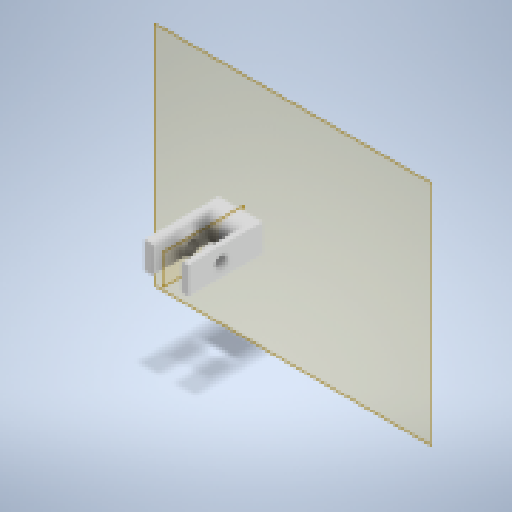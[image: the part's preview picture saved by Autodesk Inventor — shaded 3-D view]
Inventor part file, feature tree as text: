
AUTODESK INVENTOR PART (.ipt)
format: ipt  version: 2024 (Build 280153000, 153)  size: 782,848 bytes
history: native  units: mm
features: extrude x6, sketch x6, projected_geometry x5, other x5, fillet x4, reference x3, plane x2, direct_edit x1, move_body x1
ambient origin geometry x8: Origin, YZ Plane, XZ Plane, XY Plane, X Axis, Y Axis, Z Axis, Center Point
bodies: Solid1 (feature_tree)
feature tree (33):
  plane  "Work Plane1"
  extrude  "Extrusion1"  Depth=2.0mm TaperAngle=0.0deg
  extrude  "Extrusion2"  Depth=0.2mm
  extrude  "Extrusion3"  Depth=10.0mm
  fillet  "Fillet2"  Radius=10.0mm
  fillet  "Fillet3"  Radius=2.6mm
  extrude  "Extrusion4"  Depth=4.0mm
  extrude  "Extrusion5"  Depth=0.3mm
  fillet  "Fillet4"  Radius=2.0mm
  plane  "Work Plane2"
  extrude  "Extrusion6"  Depth=2.75mm
  fillet  "Fillet5"  [1 undecoded]
  direct_edit  "Direct Edit1"
  sketch  "Sketch1"  dims[d4=8.0mm d5=0.0mm d6=2.0mm d7=0.0mm]
  reference  "Reference1"
  sketch  "Sketch2"  dims[d11=0.4mm d12=0.2mm]
  projected_geometry  "Projected Loop1"
  reference  "Reference2"
  sketch  "Sketch3"  dims[d13=2.0mm d14=10.0mm d15=10.0mm d16=2.6mm]
  projected_geometry  "Projected Loop2"
  sketch  "Sketch4"  dims[d17=19.0mm d18=0.0mm d19=4.0mm]
  projected_geometry  "Projected Loop3"
  reference  "Reference3"
  sketch  "Sketch5"  dims[d20=1.0mm d21=0.3mm d22=2.0mm]
  projected_geometry  "Projected Loop4"
  sketch  "Sketch6"  dims[d23=3.9mm d25=5.0mm d26=0.0mm d27=0.0mm d28=11.7mm d29=1.5mm d30=2.0mm d31=0.0mm d32=2.75mm d33=1.5mm d34=2.0mm d35=0.0mm d36=2.75mm d37=0.0mm d38=0.0mm d39=2.5mm]
  projected_geometry  "Projected Loop5"
  other  "<userpath>\Documents\Inventor\robot arm\arms\arms.iam"
  other  "arms.iam"
  other  "base-tensioner:1"
  other  "base:1"
  other  "bearing for tensioner head:1"
  move_body  "Move1"
note: 1 required parameter value undecoded (feature->parameter linkage not recoverable at this tier; creation-order binding heuristic only, values carry confidence <= 0.55)
